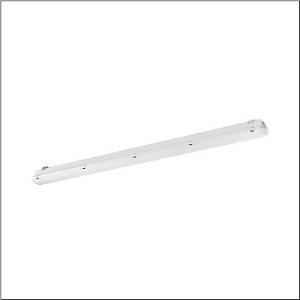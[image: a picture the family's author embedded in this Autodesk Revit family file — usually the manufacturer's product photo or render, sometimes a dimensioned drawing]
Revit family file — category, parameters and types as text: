
# Revit family: monsun_11xtreme_mo_51fe10dp440m
name_source: partatom
category: Lighting Fixtures
units: mm (PartAtom-declared; Revit-internal decimal feet)

## family parameters
Cut with Voids When Loaded = No
Host = Face
Light Source = No
Part Type = Normal
Room Calculation Point = No
Round Connector Dimension = Use Diameter
Shared = No

## types (1)
- --- (1 x LED, 4200 lm, 22.3 W, 4000K)
    Apparent Load = 22 VA
    CIE Flux Codes = 47 77 93 94 100
    Color Rendering = 80
    Color Temperature = 4000K
    Default Elevation = 1800 mm
    Description = Monsun 11Xtreme MO, damp-proof luminaire, chain hanger, primary optical cover: enclosure, of PMMA, light emission: direct distribution, primary light characteristic: symmetric, installation type: suspended mounting, surface-mounted, horizontal mounting, vertical mounting, LED, rated luminous flux: 4.200lm, luminous efficacy: 188lm/W, light colour: 840, colour temperature: 4000K, control gear: DALI 2, with terminal, 5-pole, max. 2.5mm², mains connection: 220..240V, AC, 50/60Hz, rated input power: 22W, luminaire housing, of glass-fibre reinforced polyester, uncoated, bright grey, incl. chain hanger, length: 1.590mm, width: 90mm, height: 88mm, clip for enclosure, of stainless steel (V2A), ceiling mounting element, of stainless steel (V2A), chain hanger, of stainless steel (V2A), protection rating (complete): IP66, insulation class (complete): insulation class I (protective earthing), certification: CE, ENEC, VDE, UKCA, protection symbol: D, impact resistance: IK04, permissible operating ambient temperature: -25..+40°C, standard: EN 50419, EN 60598-2-1, corresponds to IFS (International Featured Standards) requirements for safety and quality in the food industry, for indoor or canopied outdoor use, no direct snow, no direct sun, no direct rain, LABS conformity tested according to VDMA 24364:2018-05, contact your sales advisor before using the luminaires in applications with unclear chemical exposure, large temperature fluctuations or condensation-forming humidity, packaging unit: 1 piece
    Height = 88 mm
    Lamp = 1 x LED
    Lamp Light Flux = 4200 lm
    Lamp Power = 22.3 W
    Lamp count = 1
    Length = 1590 mm
    Luminous efficacy = 188 lm/W
    Manufacturer = Siteco
    ModVariant = No
    Model = 51FE10DP440M
    Mounting Place = Ceiling
    Mounting Type = Surface mounted
    Number of Poles = 1
    OnlyDefault = Yes
    Power Factor = 1
    Product Name = Monsun 11Xtreme MO
    Product group = damp-proof luminaire
    ProductGroupID = 300
    Protection Class = Protection class I
    Protection Degree = IP 66
    RLX_Detail_Level = 1
    RLX_Emergency_Light_Flux = 0 lm
    RLX_Emergency_Type = 0
    RLX_Emergency_Type_DB = No
    RlxData = <blob elided: 87077 chars, md5=b19f3a50>
    Socket = socket
    Standby Power = 0 W
    System Light Flux = 4200 lm
    System Power = 22 W
    Type Comments = factory setting: luminous flux: 100 % | dim-lin: 254 | 149 mA
    Type Image = l_1349234.jpg
    URL = http://relux.com
    VarID = @adj_033643
    Voltage = 0 V
    Weight = 0.00 kg
    Width = 90 mm

## geometry (parser evidence)
native form markers: Blend x4, Sweep x15
no freeform markers — native parametric forms only
